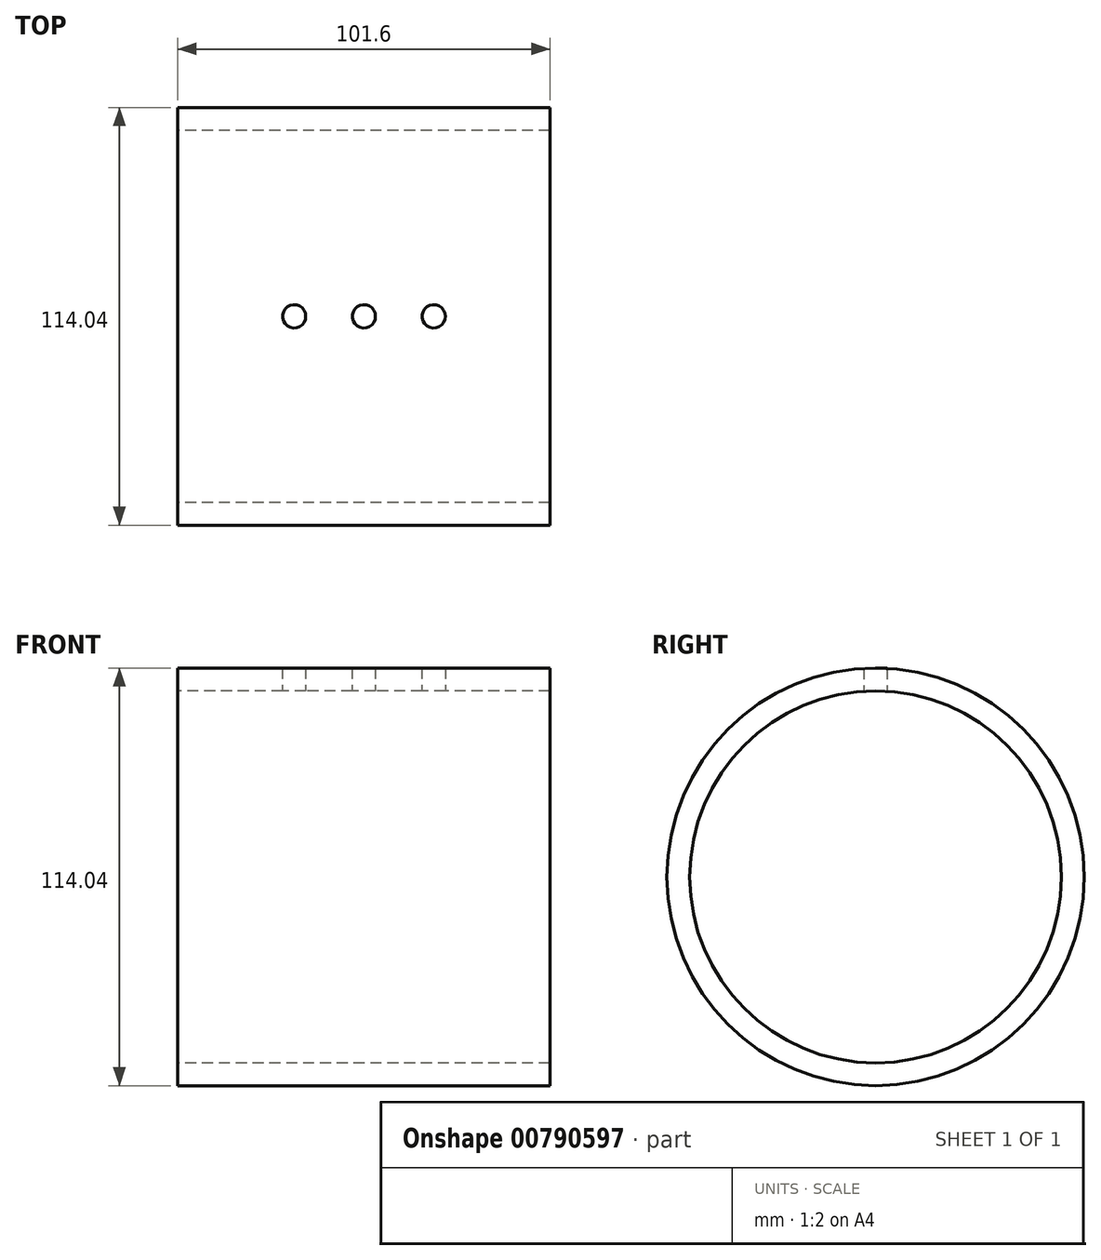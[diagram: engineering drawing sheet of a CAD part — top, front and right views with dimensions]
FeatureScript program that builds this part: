
annotation { "Feature Type Name" : "Feature", "Feature Type Description" : "" }
export const myFeature = defineFeature(function(context is Context, id is Id, definition is map)
    precondition{}
    {
        {
            var Q0;
            Q0=qCreatedBy(makeId("Right.planeOp"),FACE);
            var sketch = newSketch(context, id + "F0", { "sketchPlane" : qUnion([Q0])});
            skCircle(sketch, "E0", {"center": v(0, 0) * mm, "radius": 57.02 * mm});
            skCircle(sketch, "E1", {"center": v(0, 0) * mm, "radius": 50.8 * mm});
            skSolve(sketch);
        }
        {
            var Q0;
            Q0=makeQuery(id+"F0.imprint","IMPRINT",FACE,{"disambiguationData":[TD([[makeQuery(id+"F0.imprint","IMPRINT",EDGE,{"derivedFrom":sQuery(id+"F0.wireOp",EDGE,"E0")}),1.0]])]});
            extrude(context, id + "F1", {"entities" : qUnion([Q0]), "depth" : 101.6 * mm, "offsetDistance" : 25.4 * mm});
        }
        {
            var Q0;
            Q0=qCreatedBy(makeId("Top.planeOp"),FACE);
            var sketch = newSketch(context, id + "F2", { "sketchPlane" : qUnion([Q0])});
            skLineSegment(sketch, "E2", {"start": v(0, 0) * mm, "end": v(101.6, 0) * mm});
            skCircle(sketch, "E3", {"center": v(31.75, 0) * mm, "radius": 3.18 * mm});
            skCircle(sketch, "E4", {"center": v(50.8, 0) * mm, "radius": 3.18 * mm});
            skCircle(sketch, "E5", {"center": v(69.85, 0) * mm, "radius": 3.18 * mm});
            skLineSegment(sketch, "E6", {"start": v(31.75, 0) * mm, "end": v(0, 0) * mm});
            skSolve(sketch);
        }
        {
            var Q0;
            {var subQ0=sQuery(id+"F2.wireOp",EDGE,"E5");var subQ1=sQuery(id+"F2.wireOp",EDGE,"E2");var subQ2=makeQuery(id+"F2.imprint","INTERSECT",VERTEX,{"disambiguationData":[OD(0.0)],"derivedFrom":[subQ1,subQ0]});var subQ4=makeQuery(id+"F2.imprint","IMPRINT",EDGE,{"disambiguationData":[TD([[subQ2,-1.0]])],"derivedFrom":subQ1});var subQ5=sQuery(id+"F2.wireOp",EDGE,"E4");var subQ6=makeQuery(id+"F2.imprint","INTERSECT",VERTEX,{"disambiguationData":[OD(0.0)],"derivedFrom":[subQ1,subQ5]});var subQ8=makeQuery(id+"F2.imprint","IMPRINT",EDGE,{"disambiguationData":[TD([[subQ6,-1.0]])],"derivedFrom":subQ1});var subQ9=makeQuery(id+"F2.imprint","IMPRINT",VERTEX,{"derivedFrom":subQ1});var subQ12=makeQuery(id+"F2.imprint","IMPRINT",EDGE,{"disambiguationData":[TD([[subQ9,1.0]])],"derivedFrom":subQ1});Q0=qUnion([makeQuery(id+"F2.imprint","IMPRINT",FACE,{"disambiguationData":[TD([[subQ12,1.0]])]}),makeQuery(id+"F2.imprint","IMPRINT",FACE,{"disambiguationData":[TD([[subQ12,-1.0]])]}),makeQuery(id+"F2.imprint","IMPRINT",FACE,{"disambiguationData":[TD([[subQ8,1.0]])]}),makeQuery(id+"F2.imprint","IMPRINT",FACE,{"disambiguationData":[TD([[subQ8,-1.0]])]}),makeQuery(id+"F2.imprint","IMPRINT",FACE,{"disambiguationData":[TD([[subQ4,1.0]])]}),makeQuery(id+"F2.imprint","IMPRINT",FACE,{"disambiguationData":[TD([[subQ4,-1.0]])]})]);}
            extrude(context, id + "F3", {"entities" : qUnion([Q0]), "operationType" : NewBodyOperationType.REMOVE, "depth" : 127 * mm, "offsetDistance" : 25.4 * mm});
        }
    });
